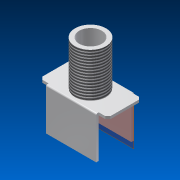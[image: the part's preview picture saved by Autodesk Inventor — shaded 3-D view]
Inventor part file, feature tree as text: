
AUTODESK INVENTOR PART (.ipt)
format: ipt  version: 2011 SP1 (Build 150282100, 282)  size: 140,288 bytes
history: native  units: mm
features: reference x5, extrude x4, sketch x4, thread x1, chamfer x1, plane x1, fillet x1
ambient origin geometry x8: Origin, YZ Plane, XZ Plane, XY Plane, X Axis, Y Axis, Z Axis, Center Point
bodies: Solid1 (feature_tree), Solid2 (feature_tree)
feature tree (17):
  extrude  "Extrusion3"  Depth=4.3mm
  extrude  "Extrusion2"  Depth=10.0mm TaperAngle=0.0deg
  thread  "Thread1"  [1 undecoded]
  chamfer  "Chamfer1"  Distance=0.5mm
  extrude  "Extrusion4"  Depth=8.0mm
  plane  "Work Plane1"
  extrude  "Extrusion5"  Depth=0.5mm TaperAngle=0.0deg
  fillet  "Fillet1"  Radius=0.5mm
  sketch  "Sketch1"  dims[d3=5.9mm d5=4.3mm]
  reference  "Reference1"
  sketch  "Sketch2"  dims[d6=8.4mm d7=0.0mm d8=10.0mm d9=0.0mm d10=0.5mm d11=2.0mm d12=45.0deg]
  sketch  "Sketch3"  dims[d13=0.3mm]
  reference  "Reference2"
  reference  "Reference3"
  sketch  "Sketch4"  dims[d15=0.3mm d16=0.5mm d17=0.0mm d18=8.0mm d19=0.5mm d20=0.0mm d21=0.5mm d22=0.0mm d23=0.25mm]
  reference  "Reference4"
  reference  "Reference5"
note: 1 required parameter value undecoded (feature->parameter linkage not recoverable at this tier; creation-order binding heuristic only, values carry confidence <= 0.55)
